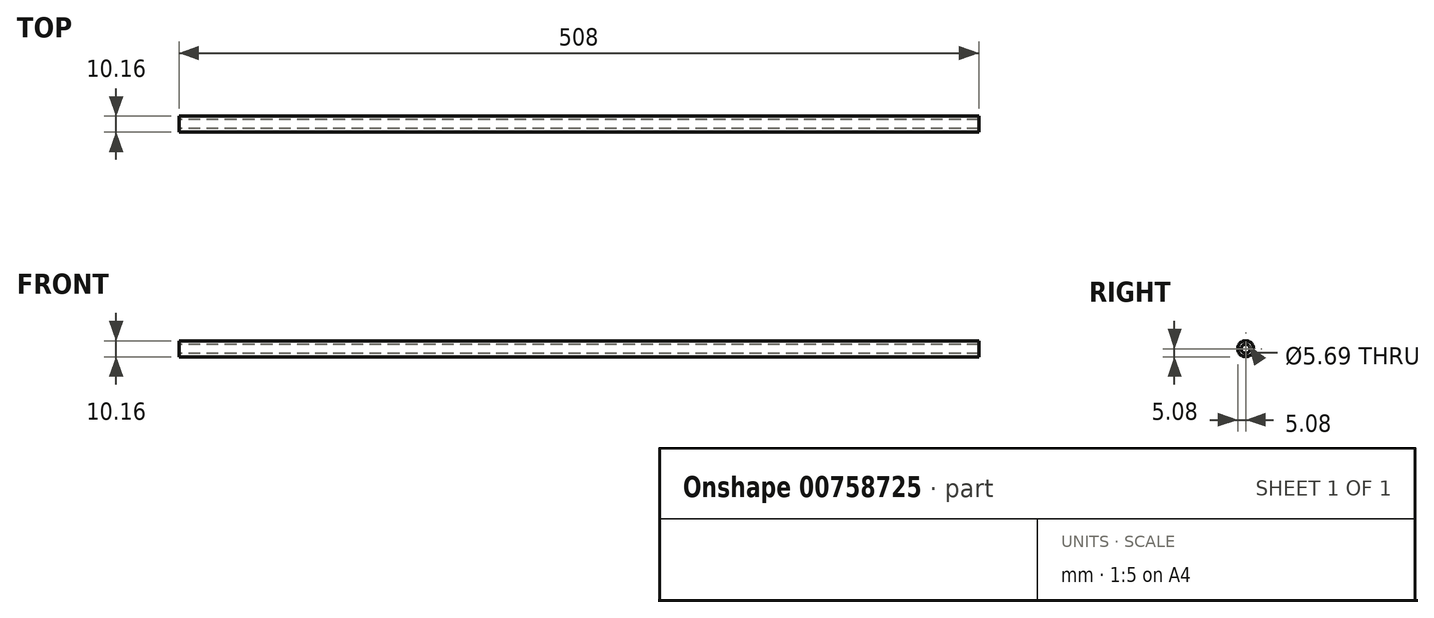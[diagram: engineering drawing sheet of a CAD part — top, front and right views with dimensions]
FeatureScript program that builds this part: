
annotation { "Feature Type Name" : "Feature", "Feature Type Description" : "" }
export const myFeature = defineFeature(function(context is Context, id is Id, definition is map)
    precondition{}
    {
        {
            var Q0;
            Q0=qCreatedBy(makeId("Right.planeOp"),FACE);
            var sketch = newSketch(context, id + "F0", { "sketchPlane" : qUnion([Q0])});
            skCircle(sketch, "E0", {"center": v(0, 0) * mm, "radius": 2.84 * mm});
            skCircle(sketch, "E1", {"center": v(0, 0) * mm, "radius": 5.08 * mm});
            skSolve(sketch);
        }
        {
            var Q0;
            Q0=makeQuery(id+"F0.imprint","IMPRINT",FACE,{"disambiguationData":[TD([[makeQuery(id+"F0.imprint","IMPRINT",EDGE,{"derivedFrom":sQuery(id+"F0.wireOp",EDGE,"E0")}),-1.0]])]});
            extrude(context, id + "F1", {"entities" : qUnion([Q0]), "depth" : 508 * mm, "offsetDistance" : 25.4 * mm});
        }
    });
